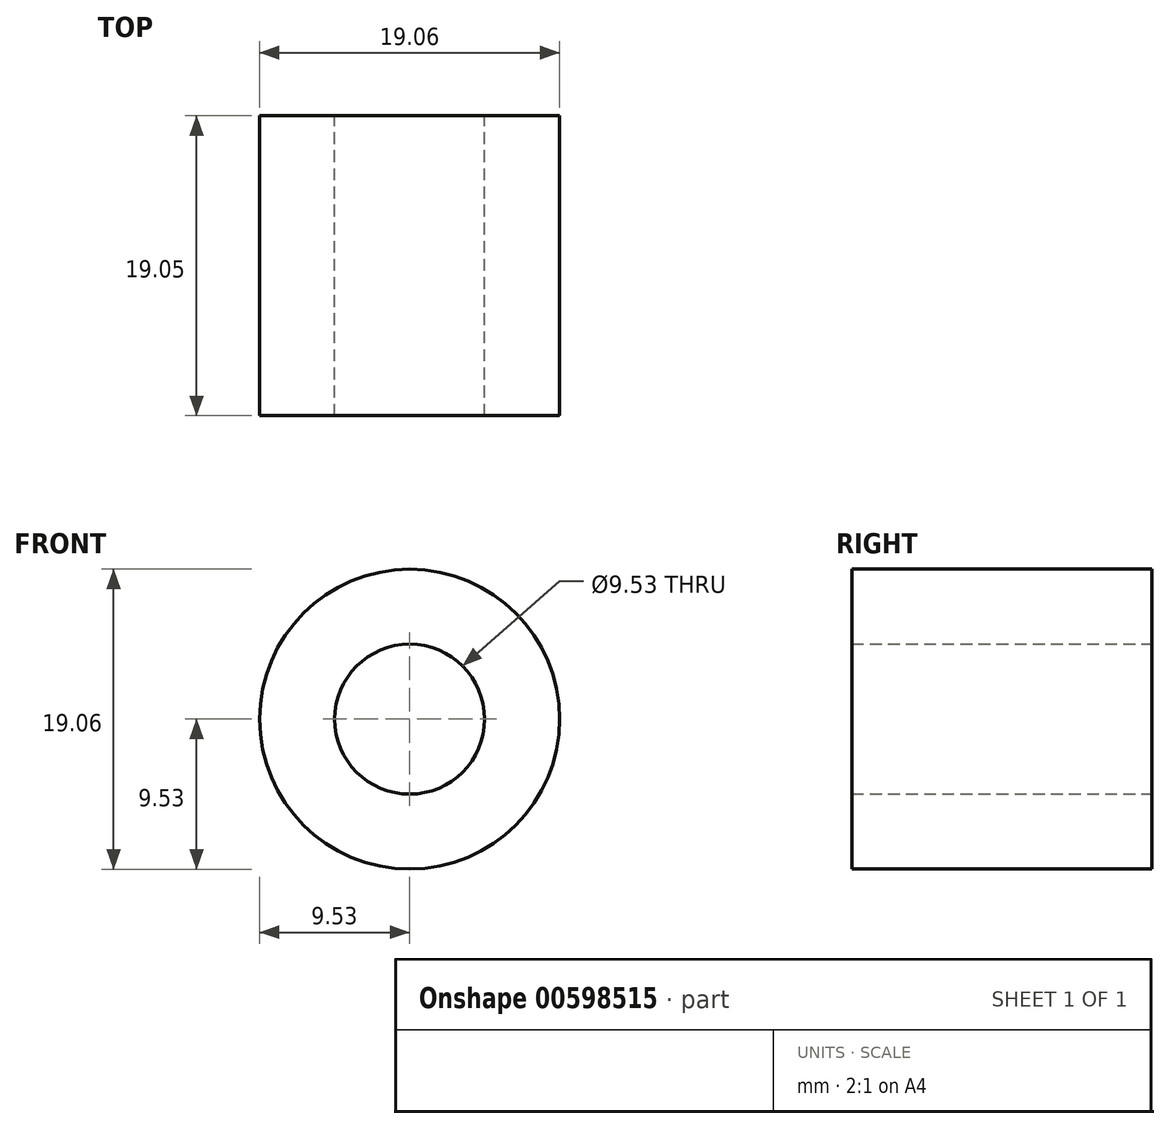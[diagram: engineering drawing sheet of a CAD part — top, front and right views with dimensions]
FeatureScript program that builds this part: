
annotation { "Feature Type Name" : "Feature", "Feature Type Description" : "" }
export const myFeature = defineFeature(function(context is Context, id is Id, definition is map)
    precondition{}
    {
        {
            var Q0;
            Q0=qCreatedBy(makeId("Front.planeOp"),FACE);
            var sketch = newSketch(context, id + "F0", { "sketchPlane" : qUnion([Q0])});
            skCircle(sketch, "E0", {"center": v(0, 0) * mm, "radius": 9.53 * mm});
            skCircle(sketch, "E1", {"center": v(0, 0) * mm, "radius": 4.76 * mm});
            skSolve(sketch);
        }
        {
            var Q0;
            Q0=makeQuery(id+"F0.imprint","IMPRINT",FACE,{"disambiguationData":[TD([[makeQuery(id+"F0.imprint","IMPRINT",EDGE,{"derivedFrom":sQuery(id+"F0.wireOp",EDGE,"E0")}),1.0]])]});
            extrude(context, id + "F1", {"entities" : qUnion([Q0]), "depth" : 19.05 * mm, "offsetDistance" : 25.4 * mm});
        }
    });
